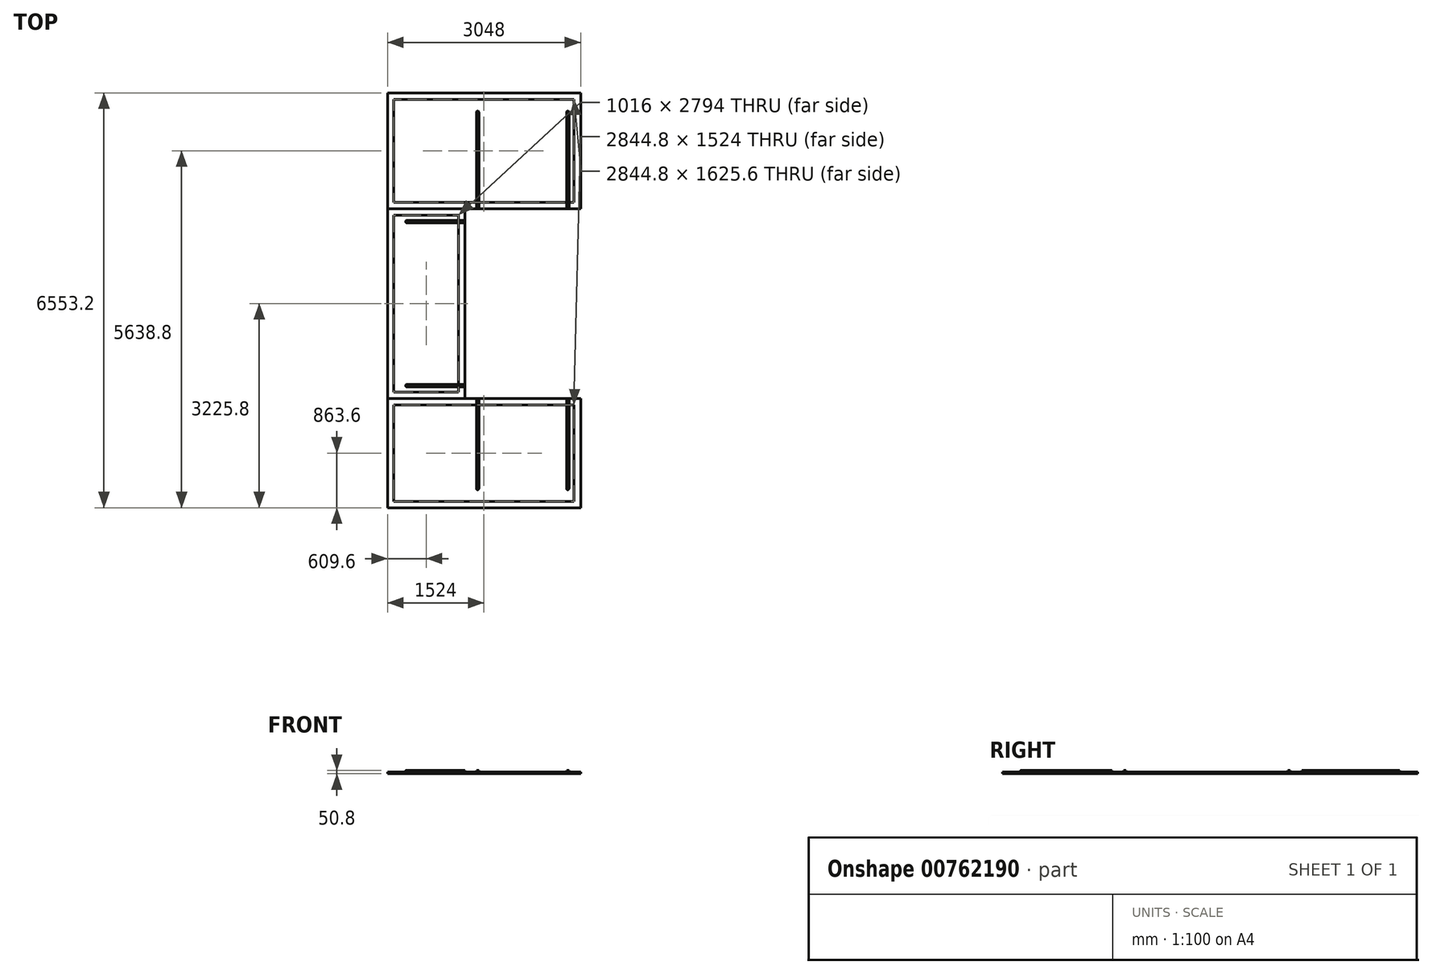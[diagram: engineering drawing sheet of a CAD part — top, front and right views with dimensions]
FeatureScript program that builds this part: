
annotation { "Feature Type Name" : "Feature", "Feature Type Description" : "" }
export const myFeature = defineFeature(function(context is Context, id is Id, definition is map)
    precondition{}
    {
        {
            var Q0;
            Q0=qCreatedBy(makeId("Top.planeOp"),FACE);
            var sketch = newSketch(context, id + "F0", { "sketchPlane" : qUnion([Q0])});
            skLineSegment(sketch, "E0.bottom", {"start": v(0, 0) * mm, "end": v(3048, 0) * mm});
            skLineSegment(sketch, "E0.top", {"start": v(0, -6553.2) * mm, "end": v(3048, -6553.2) * mm});
            skLineSegment(sketch, "E0.left", {"start": v(0, 0) * mm, "end": v(0, -6553.2) * mm});
            skLineSegment(sketch, "E0.right", {"start": v(3048, 0) * mm, "end": v(3048, -1828.8) * mm});
            skLineSegment(sketch, "E1.bottom", {"start": v(101.6, -101.6) * mm, "end": v(2946.4, -101.6) * mm});
            skLineSegment(sketch, "E1.top", {"start": v(101.6, -6451.6) * mm, "end": v(2946.4, -6451.6) * mm});
            skLineSegment(sketch, "E1.left", {"start": v(101.6, -101.6) * mm, "end": v(101.6, -1727.2) * mm});
            skLineSegment(sketch, "E1.right", {"start": v(2946.4, -101.6) * mm, "end": v(2946.4, -1727.2) * mm});
            skLineSegment(sketch, "E2", {"start": v(3048, -1828.8) * mm, "end": v(1219.2, -1828.8) * mm});
            skLineSegment(sketch, "E3", {"start": v(1219.2, -1828.8) * mm, "end": v(1219.2, -4826) * mm});
            skLineSegment(sketch, "E4", {"start": v(1219.2, -4826) * mm, "end": v(3048, -4826) * mm});
            skLineSegment(sketch, "E5", {"start": v(2946.4, -4927.6) * mm, "end": v(101.6, -4927.6) * mm});
            skLineSegment(sketch, "E6", {"start": v(1219.2, -4826) * mm, "end": v(0, -4826) * mm});
            skLineSegment(sketch, "E7", {"start": v(1117.6, -4724.4) * mm, "end": v(101.6, -4724.4) * mm});
            skLineSegment(sketch, "E8", {"start": v(1117.6, -1930.4) * mm, "end": v(101.6, -1930.4) * mm});
            skLineSegment(sketch, "E9", {"start": v(1219.2, -1828.8) * mm, "end": v(0, -1828.8) * mm});
            skLineSegment(sketch, "E10", {"start": v(2946.4, -1727.2) * mm, "end": v(101.6, -1727.2) * mm});
            skLineSegment(sketch, "E11.trimOffspring", {"start": v(101.6, -1930.4) * mm, "end": v(101.6, -4724.4) * mm});
            skLineSegment(sketch, "E12.trimOffspring", {"start": v(101.6, -4927.6) * mm, "end": v(101.6, -6451.6) * mm});
            skLineSegment(sketch, "E13.trimOffspring", {"start": v(2946.4, -4927.6) * mm, "end": v(2946.4, -6451.6) * mm});
            skLineSegment(sketch, "E14", {"start": v(1117.6, -1930.4) * mm, "end": v(1117.6, -4724.4) * mm});
            skLineSegment(sketch, "E15.trimOffspring", {"start": v(3048, -4826) * mm, "end": v(3048, -6553.2) * mm});
            skSolve(sketch);
        }
        {
            var Q0;
            {var subQ2=sQuery(id+"F0.wireOp",EDGE,"E0.bottom");Q0=makeQuery(id+"F0.imprint","IMPRINT",FACE,{"disambiguationData":[TD([[makeQuery(id+"F0.imprint","IMPRINT",EDGE,{"derivedFrom":subQ2}),-1.0]])]});}
            extrude(context, id + "F1", {"entities" : qUnion([Q0]), "depth" : 25.4 * mm, "offsetDistance" : 25.4 * mm});
        }
        {
            var Q0;
            Q0=makeQuery(id+"F0.imprint","IMPRINT",FACE,{"disambiguationData":[TD([[makeQuery(id+"F0.imprint","IMPRINT",EDGE,{"derivedFrom":sQuery(id+"F0.wireOp",EDGE,"E3")}),-1.0]])]});
            extrude(context, id + "F2", {"entities" : qUnion([Q0]), "depth" : 25.4 * mm, "offsetDistance" : 25.4 * mm});
        }
        {
            var Q0;
            {var subQ0=sQuery(id+"F0.wireOp",EDGE,"E0.top");Q0=makeQuery(id+"F0.imprint","IMPRINT",FACE,{"disambiguationData":[TD([[makeQuery(id+"F0.imprint","IMPRINT",EDGE,{"derivedFrom":subQ0}),1.0]])]});}
            extrude(context, id + "F3", {"entities" : qUnion([Q0]), "depth" : 25.4 * mm, "offsetDistance" : 25.4 * mm});
        }
        {
            var Q0;
            Q0=makeQuery(id+"F1.opExtrude","CAP_FACE",FACE,{"disambiguationData":[OSD([sQuery(id+"F0.wireOp",EDGE,"E0.bottom"),sQuery(id+"F0.wireOp",EDGE,"E0.left"),sQuery(id+"F0.wireOp",EDGE,"E0.right"),sQuery(id+"F0.wireOp",EDGE,"E1.bottom"),sQuery(id+"F0.wireOp",EDGE,"E1.left"),sQuery(id+"F0.wireOp",EDGE,"E1.right"),sQuery(id+"F0.wireOp",EDGE,"E2"),sQuery(id+"F0.wireOp",EDGE,"E9"),sQuery(id+"F0.wireOp",EDGE,"E10")])],"isStart":false});
            var sketch = newSketch(context, id + "F4", { "sketchPlane" : qUnion([Q0])});
            skLineSegment(sketch, "E16.bottom", {"start": v(2825.75, -1828.8) * mm, "end": v(2863.85, -1828.8) * mm});
            skLineSegment(sketch, "E16.top", {"start": v(2825.75, -304.8) * mm, "end": v(2863.85, -304.8) * mm});
            skLineSegment(sketch, "E16.left", {"start": v(2825.75, -1828.8) * mm, "end": v(2825.75, -304.8) * mm});
            skLineSegment(sketch, "E16.right", {"start": v(2863.85, -1828.8) * mm, "end": v(2863.85, -304.8) * mm});
            skLineSegment(sketch, "E17.bottom", {"start": v(1403.35, -1828.8) * mm, "end": v(1441.45, -1828.8) * mm});
            skLineSegment(sketch, "E17.top", {"start": v(1403.35, -304.8) * mm, "end": v(1441.45, -304.8) * mm});
            skLineSegment(sketch, "E17.left", {"start": v(1403.35, -1828.8) * mm, "end": v(1403.35, -304.8) * mm});
            skLineSegment(sketch, "E17.right", {"start": v(1441.45, -1828.8) * mm, "end": v(1441.45, -304.8) * mm});
            skLineSegment(sketch, "E18.bottom", {"start": v(1219.2, -2012.95) * mm, "end": v(304.8, -2012.95) * mm});
            skLineSegment(sketch, "E18.top", {"start": v(1219.2, -2051.05) * mm, "end": v(304.8, -2051.05) * mm});
            skLineSegment(sketch, "E18.left", {"start": v(1219.2, -2012.95) * mm, "end": v(1219.2, -2051.05) * mm});
            skLineSegment(sketch, "E18.right", {"start": v(304.8, -2012.95) * mm, "end": v(304.8, -2051.05) * mm});
            skLineSegment(sketch, "E19.bottom", {"start": v(1219.2, -4603.75) * mm, "end": v(304.8, -4603.75) * mm});
            skLineSegment(sketch, "E19.top", {"start": v(1219.2, -4641.85) * mm, "end": v(304.8, -4641.85) * mm});
            skLineSegment(sketch, "E19.left", {"start": v(1219.2, -4603.75) * mm, "end": v(1219.2, -4641.85) * mm});
            skLineSegment(sketch, "E19.right", {"start": v(304.8, -4603.75) * mm, "end": v(304.8, -4641.85) * mm});
            skLineSegment(sketch, "E20.bottom", {"start": v(1403.35, -4826) * mm, "end": v(1441.45, -4826) * mm});
            skLineSegment(sketch, "E20.top", {"start": v(1403.35, -6248.4) * mm, "end": v(1441.45, -6248.4) * mm});
            skLineSegment(sketch, "E20.left", {"start": v(1403.35, -4826) * mm, "end": v(1403.35, -6248.4) * mm});
            skLineSegment(sketch, "E20.right", {"start": v(1441.45, -4826) * mm, "end": v(1441.45, -6248.4) * mm});
            skLineSegment(sketch, "E21.bottom", {"start": v(2825.75, -4826) * mm, "end": v(2863.85, -4826) * mm});
            skLineSegment(sketch, "E21.top", {"start": v(2825.75, -6248.4) * mm, "end": v(2863.85, -6248.4) * mm});
            skLineSegment(sketch, "E21.left", {"start": v(2825.75, -4826) * mm, "end": v(2825.75, -6248.4) * mm});
            skLineSegment(sketch, "E21.right", {"start": v(2863.85, -4826) * mm, "end": v(2863.85, -6248.4) * mm});
            skCircle(sketch, "E22", {"center": v(2844.8, -304.8) * mm, "radius": 19.05 * mm});
            skCircle(sketch, "E23", {"center": v(1422.4, -304.8) * mm, "radius": 19.05 * mm});
            skCircle(sketch, "E24", {"center": v(304.8, -2032) * mm, "radius": 19.05 * mm});
            skCircle(sketch, "E25", {"center": v(304.8, -4622.8) * mm, "radius": 19.05 * mm});
            skCircle(sketch, "E26", {"center": v(1422.4, -6248.4) * mm, "radius": 19.05 * mm});
            skCircle(sketch, "E27", {"center": v(2844.8, -6248.4) * mm, "radius": 19.05 * mm});
            skSolve(sketch);
        }
        {
            var Q0;
            Q0 = qSketchRegion(id + "F4", true);
            extrude(context, id + "F5", {"entities" : qUnion([Q0]), "depth" : 25.4 * mm, "offsetDistance" : 25.4 * mm});
        }
    });
